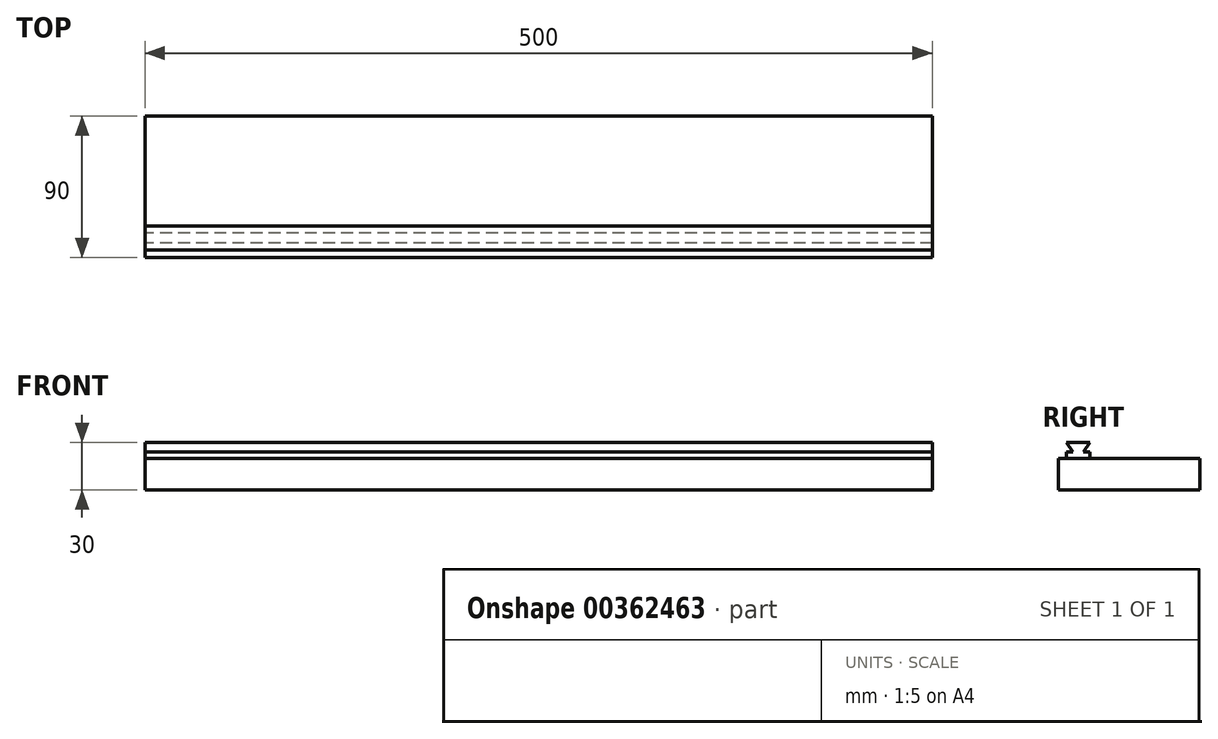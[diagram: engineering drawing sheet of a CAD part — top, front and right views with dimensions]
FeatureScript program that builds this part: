
annotation { "Feature Type Name" : "Feature", "Feature Type Description" : "" }
export const myFeature = defineFeature(function(context is Context, id is Id, definition is map)
    precondition{}
    {
        {
            var Q0;
            Q0=qCreatedBy(makeId("Top.planeOp"),FACE);
            var sketch = newSketch(context, id + "F0", { "sketchPlane" : qUnion([Q0])});
            skLineSegment(sketch, "E0.bottom", {"start": v(0, 0) * mm, "end": v(500, 0) * mm});
            skLineSegment(sketch, "E0.top", {"start": v(0, 90) * mm, "end": v(500, 90) * mm});
            skLineSegment(sketch, "E0.left", {"start": v(0, 0) * mm, "end": v(0, 90) * mm});
            skLineSegment(sketch, "E0.right", {"start": v(500, 0) * mm, "end": v(500, 90) * mm});
            skSolve(sketch);
        }
        {
            var Q0;
            Q0=makeQuery(id+"F0.imprint","IMPRINT",FACE,{"disambiguationData":[TD([[makeQuery(id+"F0.imprint","IMPRINT",EDGE,{"derivedFrom":sQuery(id+"F0.wireOp",EDGE,"E0.bottom")}),1.0]])]});
            extrude(context, id + "F1", {"entities" : qUnion([Q0]), "depth" : 20 * mm, "offsetDistance" : 25 * mm});
        }
        {
            var Q0;
            Q0=qCreatedBy(makeId("Right.planeOp"),FACE);
            var sketch = newSketch(context, id + "F2", { "sketchPlane" : qUnion([Q0])});
            skLineSegment(sketch, "E1.bottom", {"start": v(20, 20) * mm, "end": v(5, 20) * mm});
            skLineSegment(sketch, "E1.top", {"start": v(20, 24) * mm, "end": v(15.8, 24) * mm});
            skLineSegment(sketch, "E1.left", {"start": v(20, 20) * mm, "end": v(20, 24) * mm});
            skLineSegment(sketch, "E1.right", {"start": v(5, 20) * mm, "end": v(5, 24) * mm});
            skLineSegment(sketch, "E2", {"start": v(20, 30) * mm, "end": v(5, 30) * mm});
            skLineSegment(sketch, "E3", {"start": v(20, 30) * mm, "end": v(15.8, 24) * mm});
            skLineSegment(sketch, "E4", {"start": v(5, 30) * mm, "end": v(9.2, 24) * mm});
            skLineSegment(sketch, "E5.trimOffspring", {"start": v(9.2, 24) * mm, "end": v(5, 24) * mm});
            skSolve(sketch);
        }
        {
            var Q0;
            Q0 = qSketchRegion(id + "F2", true);
            extrude(context, id + "F3", {"entities" : qUnion([Q0]), "depth" : 500 * mm, "offsetDistance" : 25 * mm});
        }
    });
